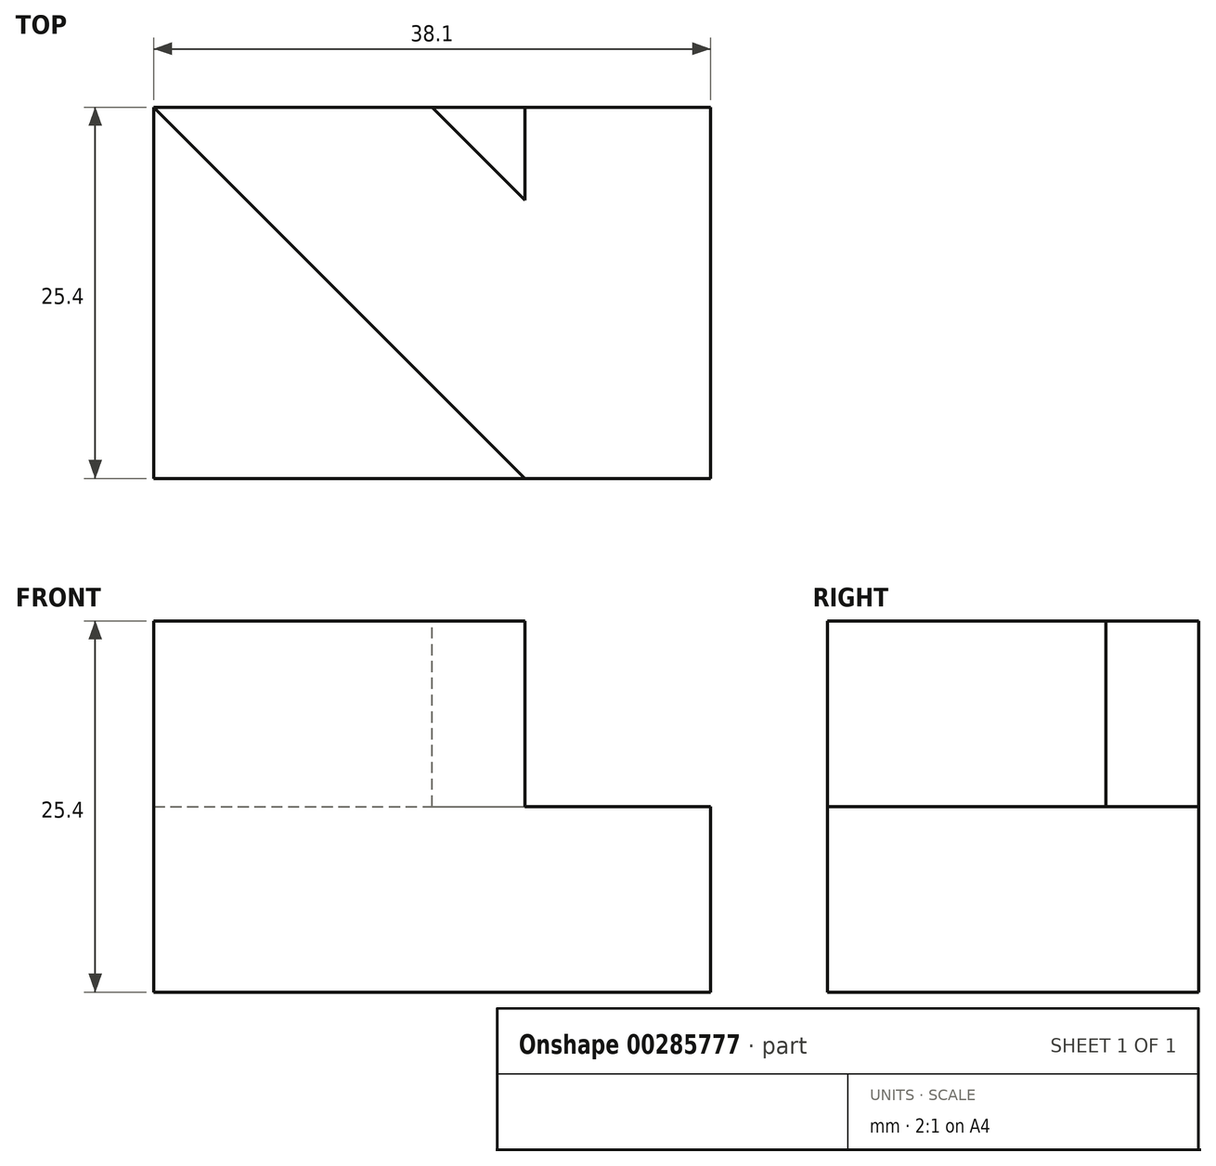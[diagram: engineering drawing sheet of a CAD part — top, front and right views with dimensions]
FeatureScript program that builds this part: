
annotation { "Feature Type Name" : "Feature", "Feature Type Description" : "" }
export const myFeature = defineFeature(function(context is Context, id is Id, definition is map)
    precondition{}
    {
        {
            var Q0;
            Q0=qCreatedBy(makeId("Front.planeOp"),FACE);
            var sketch = newSketch(context, id + "F0", { "sketchPlane" : qUnion([Q0])});
            skLineSegment(sketch, "E0.bottom", {"start": v(0, 0) * mm, "end": v(38.1, 0) * mm});
            skLineSegment(sketch, "E0.top", {"start": v(0, 25.4) * mm, "end": v(38.1, 25.4) * mm});
            skLineSegment(sketch, "E0.left", {"start": v(0, 0) * mm, "end": v(0, 25.4) * mm});
            skLineSegment(sketch, "E0.right", {"start": v(38.1, 0) * mm, "end": v(38.1, 25.4) * mm});
            skLineSegment(sketch, "E1", {"start": v(38.1, 25.4) * mm, "end": v(25.4, 25.4) * mm});
            skLineSegment(sketch, "E2", {"start": v(25.4, 25.4) * mm, "end": v(25.4, 12.7) * mm});
            skLineSegment(sketch, "E3", {"start": v(25.4, 12.7) * mm, "end": v(38.1, 12.7) * mm});
            skLineSegment(sketch, "E4", {"start": v(38.1, 12.7) * mm, "end": v(38.1, 25.4) * mm});
            skSolve(sketch);
        }
        {
            var Q0;
            Q0=makeQuery(id+"F0.imprint","IMPRINT",FACE,{"disambiguationData":[TD([[makeQuery(id+"F0.imprint","IMPRINT",EDGE,{"derivedFrom":sQuery(id+"F0.wireOp",EDGE,"E0.bottom")}),1.0]])]});
            var Q1;
            Q1=makeQuery(id+"F0.imprint","IMPRINT",FACE,{"disambiguationData":[TD([[makeQuery(id+"F0.imprint","IMPRINT",EDGE,{"derivedFrom":sQuery(id+"F0.wireOp",EDGE,"E1")}),1.0]])]});
            extrude(context, id + "F1", {"entities" : qUnion([Q0, Q1]), "depth" : 25.4 * mm});
        }
        {
            var Q0;
            Q0=makeQuery(id+"F1.opExtrude","SWEPT_FACE",FACE,{"disambiguationData":[OSD([sQuery(id+"F0.wireOp",EDGE,"E0.top"),sQuery(id+"F0.wireOp",EDGE,"E1")])]});
            var sketch = newSketch(context, id + "F2", { "sketchPlane" : qUnion([Q0])});
            skLineSegment(sketch, "E5", {"start": v(0, 0) * mm, "end": v(25.4, -25.4) * mm});
            skLineSegment(sketch, "E6", {"start": v(19.05, 0) * mm, "end": v(38.1, -19.05) * mm});
            skSolve(sketch);
        }
        {
            var Q0;
            {var subQ6=sQuery(id+"F2.wireOp",EDGE,"E5");Q0=makeQuery(id+"F2.imprint","IMPRINT",FACE,{"disambiguationData":[TD([[makeQuery(id+"F2.imprint","IMPRINT",EDGE,{"derivedFrom":subQ6}),1.0]])]});}
            extrude(context, id + "F3", {"entities" : qUnion([Q0]), "operationType" : NewBodyOperationType.REMOVE, "oppositeDirection" : true, "depth" : 12.7 * mm});
        }
    });
